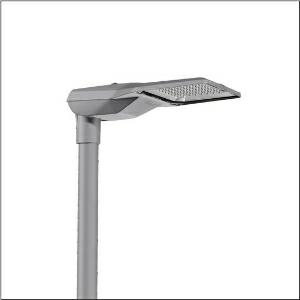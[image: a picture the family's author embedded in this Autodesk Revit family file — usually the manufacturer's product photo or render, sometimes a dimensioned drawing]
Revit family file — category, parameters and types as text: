
# Revit family: streetlight_sl_21_midi___st0_8a_5xe3c43s08mb_603c
name_source: partatom
category: Lighting Fixtures
units: mm (PartAtom-declared; Revit-internal decimal feet)

## family parameters
Cut with Voids When Loaded = No
Host = Face
Light Source = No
Part Type = Normal
Room Calculation Point = No
Round Connector Dimension = Use Diameter
Shared = No

## types (1)
- --- (1 x LED, 20180 lm, 147 W, 4000K)
    Apparent Load = 147 VA
    CIE Flux Codes = 38 75 97 100 100
    Color Rendering = 70
    Color Temperature = 4000K
    Default Elevation = 1800 mm
    Description = Streetlight SL 21 midi, mast luminaire, primary light control with lens, of PMMA, primary optical cover: cover, of toughened safety glass, transparent, light distribution: ST0.8a, light emission: direct distribution, primary light characteristic: asymmetric, installation type: side-entry, post-top, LED, High Power LED, rated luminous flux: 20.180lm, luminous efficacy: 137lm/W, light colour: 740, colour temperature: 4000K, control gear: D4i, control: overheat protection, constant luminous flux control, time-dependent luminous flux control, flexible luminous flux parameterisation, pre-setting: logarithmic dimming characteristic, mains connection: 230..240V, AC, 50/60Hz, start of lifetime: 147W, end of service life: 155W, reduction: 65W, luminaire housing, of diecast aluminium, powder-coated, SITECO metallic grey (DB 702S), corrosivity category C5 high according to DIN EN ISO 12944, please order mast flange separately, inclination adjustable: 0°, 5°, 10°, 15°, sealing non-destructively replaceable, multi-level sealing system, length: 644mm, width: 335mm, height: 110mm, mast flange for spigot size: 42mm (side-entry): 5XC10008XM4, 60/48mm (side-entry/post-top): 5XC10108XM2, 76/60mm (side-entry/post-top): 5XC10108XM1, mounting height: 4..8m, Smart Interface above, protection rating (complete): IP66, insulation class (complete): insulation class II (safety insulation), certification: CE, ENEC, ENEC+, VDE, impact resistance: IK10, permissible operating ambient temperature for outdoor applications: -40..+50°C, standard-compliant lighting for roads and squares, packaging unit: 1 piece

Light Distribution: ST0.8a
    Height = 111 mm
    Lamp = 1 x LED
    Lamp Light Flux = 20180 lm
    Lamp Power = 147 W
    Lamp count = 1
    Length = 644 mm
    Luminous efficacy = 137 lm/W
    Manufacturer = Siteco
    ModVariant = No
    Model = 5XE3C43S08MB
    Number of Poles = 1
    OnlyDefault = Yes
    Power Factor = 1
    Product Name = Streetlight SL 21 midi | ST0.8a
    Product group = mast luminaire | pylon top
    ProductGroupID = 6100
    Protection Class = Protection class II
    Protection Degree = IP 66
    RLX_Detail_Level = 1
    RLX_Emergency_Light_Flux = 0 lm
    RLX_Emergency_Type = 0
    RLX_Emergency_Type_DB = No
    RlxData = <blob elided: 26925 chars, md5=39131e37>
    Socket = socket
    Standby Power = 0 W
    System Light Flux = 20180 lm
    System Power = 147 W
    Type Comments = factory setting: luminous flux: 100 % | dim-lin: 254 | 750 mA
    Type Image = l_1004302.jpg
    URL = http://relux.com
    VarID = @adj_183531
    Voltage = 0 V
    Weight = 0.00 kg
    Width = 336 mm

## geometry (parser evidence)
native form markers: Blend x4, Sweep x12
no freeform markers — native parametric forms only
